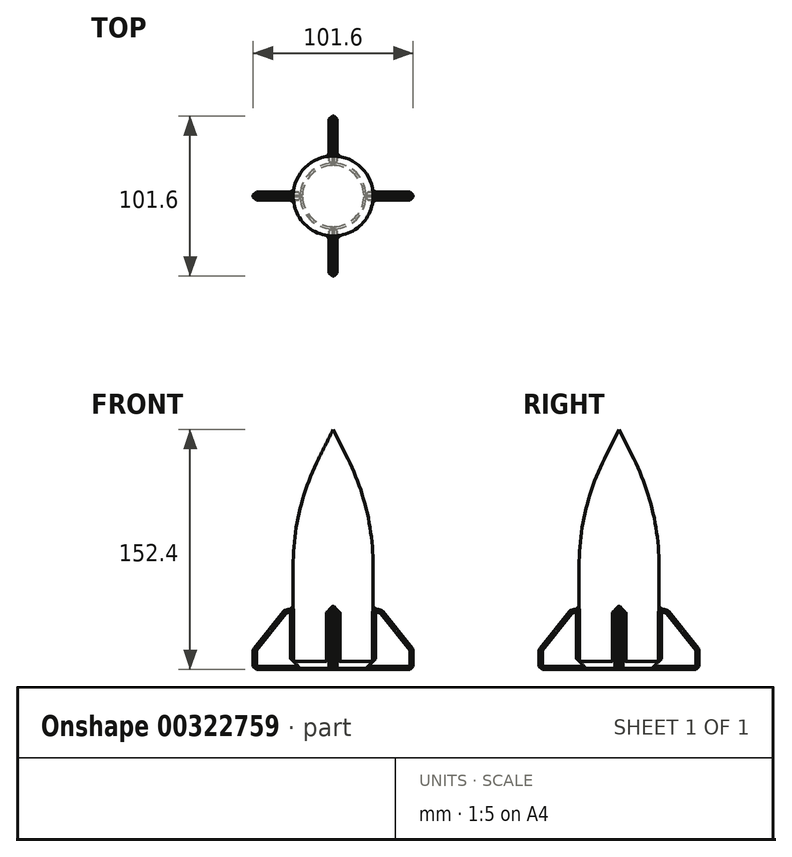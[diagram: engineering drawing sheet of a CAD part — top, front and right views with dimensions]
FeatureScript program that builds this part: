
annotation { "Feature Type Name" : "Feature", "Feature Type Description" : "" }
export const myFeature = defineFeature(function(context is Context, id is Id, definition is map)
    precondition{}
    {
        {
            var Q0;
            Q0=qCreatedBy(makeId("Top.planeOp"),FACE);
            var sketch = newSketch(context, id + "F0", { "sketchPlane" : qUnion([Q0])});
            skLineSegment(sketch, "E0.bottom", {"start": v(-25.4, 25.4) * mm, "end": v(25.4, 25.4) * mm});
            skLineSegment(sketch, "E0.top", {"start": v(-25.4, -25.4) * mm, "end": v(25.4, -25.4) * mm});
            skLineSegment(sketch, "E0.left", {"start": v(-25.4, 25.4) * mm, "end": v(-25.4, -25.4) * mm});
            skLineSegment(sketch, "E0.right", {"start": v(25.4, 25.4) * mm, "end": v(25.4, -25.4) * mm});
            skSolve(sketch);
        }
        {
            var Q0;
            Q0 = qSketchRegion(id + "F0", true);
            extrude(context, id + "F1", {"entities" : qUnion([Q0]), "depth" : 152.4 * mm});
        }
        {
            var Q0;
            Q0=makeQuery(id+"F1.opExtrude","SWEPT_FACE",FACE,{"disambiguationData":[OSD([sQuery(id+"F0.wireOp",EDGE,"E0.bottom")])]});
            var sketch = newSketch(context, id + "F2", { "sketchPlane" : qUnion([Q0])});
            skLineSegment(sketch, "E1.bottom", {"start": v(-2.54, 0) * mm, "end": v(2.54, 0) * mm});
            skLineSegment(sketch, "E1.top", {"start": v(-2.54, 38.1) * mm, "end": v(2.54, 38.1) * mm});
            skLineSegment(sketch, "E1.left", {"start": v(-2.54, 0) * mm, "end": v(-2.54, 38.1) * mm});
            skLineSegment(sketch, "E1.right", {"start": v(2.54, 0) * mm, "end": v(2.54, 38.1) * mm});
            skSolve(sketch);
        }
        {
            var Q0;
            Q0 = qSketchRegion(id + "F2", true);
            extrude(context, id + "F3", {"entities" : qUnion([Q0]), "operationType" : NewBodyOperationType.ADD, "depth" : 25.4 * mm});
        }
        {
            var Q0;
            Q0=makeQuery(id+"F3.opExtrude","CAP_EDGE",EDGE,{"disambiguationData":[OSD([sQuery(id+"F2.wireOp",EDGE,"E1.top")])],"isStart":false});
            chamfer(context, id + "F4", {"entities" : qUnion([Q0]), "chamferType" : ChamferType.TWO_OFFSETS, "width1" : 20.32 * mm, "oppositeDirection" : false, "width2" : 25.4 * mm, "tangentPropagation" : true});
        }
        {
            var Q0;
            Q0=makeQuery(id+"F1.opExtrude","SWEPT_FACE",FACE,{"disambiguationData":[OSD([sQuery(id+"F0.wireOp",EDGE,"E0.left")])]});
            var sketch = newSketch(context, id + "F5", { "sketchPlane" : qUnion([Q0])});
            skLineSegment(sketch, "E2.bottom", {"start": v(-2.54, 0) * mm, "end": v(2.54, 0) * mm});
            skLineSegment(sketch, "E2.top", {"start": v(-2.54, 38.1) * mm, "end": v(2.54, 38.1) * mm});
            skLineSegment(sketch, "E2.left", {"start": v(-2.54, 0) * mm, "end": v(-2.54, 38.1) * mm});
            skLineSegment(sketch, "E2.right", {"start": v(2.54, 0) * mm, "end": v(2.54, 38.1) * mm});
            skSolve(sketch);
        }
        {
            var Q0;
            Q0 = qSketchRegion(id + "F5", true);
            extrude(context, id + "F6", {"entities" : qUnion([Q0]), "operationType" : NewBodyOperationType.ADD, "depth" : 25.4 * mm});
        }
        {
            var Q0;
            Q0=makeQuery(id+"F6.opExtrude","CAP_EDGE",EDGE,{"disambiguationData":[OSD([sQuery(id+"F5.wireOp",EDGE,"E2.top")])],"isStart":false});
            chamfer(context, id + "F7", {"entities" : qUnion([Q0]), "chamferType" : ChamferType.TWO_OFFSETS, "width1" : 20.32 * mm, "oppositeDirection" : false, "width2" : 25.4 * mm, "tangentPropagation" : true});
        }
        {
            var Q0;
            Q0=makeQuery(id+"F1.opExtrude","SWEPT_FACE",FACE,{"disambiguationData":[OSD([sQuery(id+"F0.wireOp",EDGE,"E0.top")])]});
            var sketch = newSketch(context, id + "F8", { "sketchPlane" : qUnion([Q0])});
            skLineSegment(sketch, "E3.bottom", {"start": v(-2.54, 0) * mm, "end": v(2.54, 0) * mm});
            skLineSegment(sketch, "E3.top", {"start": v(-2.54, 38.1) * mm, "end": v(2.54, 38.1) * mm});
            skLineSegment(sketch, "E3.left", {"start": v(-2.54, 0) * mm, "end": v(-2.54, 38.1) * mm});
            skLineSegment(sketch, "E3.right", {"start": v(2.54, 0) * mm, "end": v(2.54, 38.1) * mm});
            skSolve(sketch);
        }
        {
            var Q0;
            Q0 = qSketchRegion(id + "F8", true);
            extrude(context, id + "F9", {"entities" : qUnion([Q0]), "operationType" : NewBodyOperationType.ADD, "depth" : 25.4 * mm});
        }
        {
            var Q0;
            Q0=makeQuery(id+"F9.opExtrude","CAP_EDGE",EDGE,{"disambiguationData":[OSD([sQuery(id+"F8.wireOp",EDGE,"E3.top")])],"isStart":false});
            chamfer(context, id + "F10", {"entities" : qUnion([Q0]), "chamferType" : ChamferType.TWO_OFFSETS, "width1" : 20.32 * mm, "oppositeDirection" : false, "width2" : 25.4 * mm, "tangentPropagation" : true});
        }
        {
            var Q0;
            Q0=makeQuery(id+"F1.opExtrude","SWEPT_FACE",FACE,{"disambiguationData":[OSD([sQuery(id+"F0.wireOp",EDGE,"E0.right")])]});
            var sketch = newSketch(context, id + "F11", { "sketchPlane" : qUnion([Q0])});
            skLineSegment(sketch, "E4.bottom", {"start": v(-2.54, 0) * mm, "end": v(2.54, 0) * mm});
            skLineSegment(sketch, "E4.top", {"start": v(-2.54, 38.1) * mm, "end": v(2.54, 38.1) * mm});
            skLineSegment(sketch, "E4.left", {"start": v(-2.54, 0) * mm, "end": v(-2.54, 38.1) * mm});
            skLineSegment(sketch, "E4.right", {"start": v(2.54, 0) * mm, "end": v(2.54, 38.1) * mm});
            skSolve(sketch);
        }
        {
            var Q0;
            Q0 = qSketchRegion(id + "F11", true);
            extrude(context, id + "F12", {"entities" : qUnion([Q0]), "operationType" : NewBodyOperationType.ADD, "depth" : 25.4 * mm});
        }
        {
            var Q0;
            Q0=makeQuery(id+"F12.opExtrude","CAP_EDGE",EDGE,{"disambiguationData":[OSD([sQuery(id+"F11.wireOp",EDGE,"E4.top")])],"isStart":false});
            chamfer(context, id + "F13", {"entities" : qUnion([Q0]), "chamferType" : ChamferType.TWO_OFFSETS, "width1" : 20.32 * mm, "oppositeDirection" : false, "width2" : 25.4 * mm, "tangentPropagation" : true});
        }
        {
            var Q0;
            Q0=makeQuery(id+"F1.opExtrude","SWEPT_EDGE",EDGE,{"disambiguationData":[OSD([sQuery(id+"F0.wireOp",EDGE,"E0.top"),sQuery(id+"F0.wireOp",EDGE,"E0.right")])]});
            var Q1;
            Q1=makeQuery(id+"F1.opExtrude","SWEPT_EDGE",EDGE,{"disambiguationData":[OSD([sQuery(id+"F0.wireOp",EDGE,"E0.top"),sQuery(id+"F0.wireOp",EDGE,"E0.left")])]});
            var Q2;
            Q2=makeQuery(id+"F1.opExtrude","SWEPT_EDGE",EDGE,{"disambiguationData":[OSD([sQuery(id+"F0.wireOp",EDGE,"E0.bottom"),sQuery(id+"F0.wireOp",EDGE,"E0.left")])]});
            var Q3;
            Q3=makeQuery(id+"F1.opExtrude","SWEPT_EDGE",EDGE,{"disambiguationData":[OSD([sQuery(id+"F0.wireOp",EDGE,"E0.bottom"),sQuery(id+"F0.wireOp",EDGE,"E0.right")])]});
            fillet(context, id + "F14", {"entities" : qUnion([Q0, Q1, Q2, Q3]), "radius" : 25.4 * mm, "tangentPropagation" : true, "allowEdgeOverflow" : false});
        }
        {
            var Q0;
            {var subQ0=sQuery(id+"F0.wireOp",EDGE,"E0.left");var subQ1=sQuery(id+"F0.wireOp",EDGE,"E0.bottom");Q0=makeQuery(id+"F14.opFillet","BLEND_EDGE",EDGE,{"blendedFrom":[makeQuery(id+"F1.opExtrude","SWEPT_EDGE",EDGE,{"disambiguationData":[OSD([subQ1,subQ0])]}),makeQuery(id+"F1.opExtrude","CAP_FACE",FACE,{"disambiguationData":[OSD([subQ1,sQuery(id+"F0.wireOp",EDGE,"E0.top"),subQ0,sQuery(id+"F0.wireOp",EDGE,"E0.right")])],"isStart":false})],"blendedInto":[makeQuery(id+"F1.opExtrude","CAP_FACE",FACE,{"disambiguationData":[OSD([subQ1,sQuery(id+"F0.wireOp",EDGE,"E0.top"),subQ0,sQuery(id+"F0.wireOp",EDGE,"E0.right")])],"isStart":false})]});}
            chamfer(context, id + "F15", {"entities" : qUnion([Q0]), "chamferType" : ChamferType.TWO_OFFSETS, "width1" : 25.4 * mm, "oppositeDirection" : false, "width2" : 50.8 * mm, "tangentPropagation" : true});
        }
        {
            var Q0;
            {var subQ0=sQuery(id+"F0.wireOp",EDGE,"E0.right");var subQ1=sQuery(id+"F0.wireOp",EDGE,"E0.bottom");var subQ2=sQuery(id+"F0.wireOp",EDGE,"E0.left");Q0=makeQuery(id+"F15.opChamfer","BLEND_EDGE",EDGE,{"blendedFrom":[makeQuery(id+"F14.opFillet","BLEND_EDGE",EDGE,{"blendedFrom":[makeQuery(id+"F1.opExtrude","SWEPT_EDGE",EDGE,{"disambiguationData":[OSD([subQ1,subQ2])]}),makeQuery(id+"F1.opExtrude","CAP_FACE",FACE,{"disambiguationData":[OSD([subQ1,sQuery(id+"F0.wireOp",EDGE,"E0.top"),subQ2,subQ0])],"isStart":false})],"blendedInto":[makeQuery(id+"F1.opExtrude","CAP_FACE",FACE,{"disambiguationData":[OSD([subQ1,sQuery(id+"F0.wireOp",EDGE,"E0.top"),subQ2,subQ0])],"isStart":false})]}),makeQuery(id+"F14.opFillet","BLEND_FACE",FACE,{"disambiguationData":[OSD([subQ1,subQ0])]})],"blendedInto":[makeQuery(id+"F14.opFillet","BLEND_FACE",FACE,{"disambiguationData":[OSD([subQ1,subQ0])]})]});}
            fillet(context, id + "F16", {"entities" : qUnion([Q0]), "radius" : 152.4 * mm, "tangentPropagation" : true, "allowEdgeOverflow" : false});
        }
        {
            var Q0;
            {var subQ0=sQuery(id+"F8.wireOp",EDGE,"E3.top");Q0=makeQuery(id+"F10.opChamfer","BLEND_EDGE",EDGE,{"blendedFrom":[makeQuery(id+"F9.opExtrude","CAP_EDGE",EDGE,{"disambiguationData":[OSD([subQ0])],"isStart":false}),makeQuery(id+"F9.opExtrude","SWEPT_FACE",FACE,{"disambiguationData":[OSD([subQ0])]})],"blendedInto":[makeQuery(id+"F9.opExtrude","SWEPT_FACE",FACE,{"disambiguationData":[OSD([subQ0])]})]});}
            chamfer(context, id + "F17", {"entities" : qUnion([Q0]), "width" : 2.54 * mm, "tangentPropagation" : true});
        }
        {
            var Q0;
            {var subQ0=sQuery(id+"F11.wireOp",EDGE,"E4.top");Q0=makeQuery(id+"F13.opChamfer","BLEND_EDGE",EDGE,{"blendedFrom":[makeQuery(id+"F12.opExtrude","CAP_EDGE",EDGE,{"disambiguationData":[OSD([subQ0])],"isStart":false}),makeQuery(id+"F12.opExtrude","SWEPT_FACE",FACE,{"disambiguationData":[OSD([subQ0])]})],"blendedInto":[makeQuery(id+"F12.opExtrude","SWEPT_FACE",FACE,{"disambiguationData":[OSD([subQ0])]})]});}
            chamfer(context, id + "F18", {"entities" : qUnion([Q0]), "width" : 2.54 * mm, "tangentPropagation" : true});
        }
        {
            var Q0;
            {var subQ0=sQuery(id+"F2.wireOp",EDGE,"E1.top");Q0=makeQuery(id+"F4.opChamfer","BLEND_EDGE",EDGE,{"blendedFrom":[makeQuery(id+"F3.opExtrude","CAP_EDGE",EDGE,{"disambiguationData":[OSD([subQ0])],"isStart":false}),makeQuery(id+"F3.opExtrude","SWEPT_FACE",FACE,{"disambiguationData":[OSD([subQ0])]})],"blendedInto":[makeQuery(id+"F3.opExtrude","SWEPT_FACE",FACE,{"disambiguationData":[OSD([subQ0])]})]});}
            var Q1;
            {var subQ0=sQuery(id+"F5.wireOp",EDGE,"E2.top");Q1=makeQuery(id+"F7.opChamfer","BLEND_EDGE",EDGE,{"blendedFrom":[makeQuery(id+"F6.opExtrude","CAP_EDGE",EDGE,{"disambiguationData":[OSD([subQ0])],"isStart":false}),makeQuery(id+"F6.opExtrude","SWEPT_FACE",FACE,{"disambiguationData":[OSD([subQ0])]})],"blendedInto":[makeQuery(id+"F6.opExtrude","SWEPT_FACE",FACE,{"disambiguationData":[OSD([subQ0])]})]});}
            chamfer(context, id + "F19", {"entities" : qUnion([Q0, Q1]), "width" : 2.54 * mm, "tangentPropagation" : true});
        }
        {
            var Q0;
            {var subQ0=sQuery(id+"F0.wireOp",EDGE,"E0.left");var subQ1=sQuery(id+"F0.wireOp",EDGE,"E0.bottom");Q0=makeQuery(id+"F14.opFillet","BLEND_EDGE",EDGE,{"blendedFrom":[makeQuery(id+"F1.opExtrude","SWEPT_EDGE",EDGE,{"disambiguationData":[OSD([subQ1,subQ0])]}),makeQuery(id+"F12.boolean.opBoolean","MERGE",FACE,{"derivedFrom":[makeQuery(id+"F9.boolean.opBoolean","MERGE",FACE,{"derivedFrom":[makeQuery(id+"F6.boolean.opBoolean","MERGE",FACE,{"derivedFrom":[makeQuery(id+"F3.boolean.opBoolean","MERGE",FACE,{"derivedFrom":[makeQuery(id+"F1.opExtrude","CAP_FACE",FACE,{"disambiguationData":[OSD([subQ1,sQuery(id+"F0.wireOp",EDGE,"E0.top"),subQ0,sQuery(id+"F0.wireOp",EDGE,"E0.right")])],"isStart":true}),makeQuery(id+"F3.opExtrude","SWEPT_FACE",FACE,{"disambiguationData":[OSD([sQuery(id+"F2.wireOp",EDGE,"E1.bottom")])]})]}),makeQuery(id+"F6.opExtrude","SWEPT_FACE",FACE,{"disambiguationData":[OSD([sQuery(id+"F5.wireOp",EDGE,"E2.bottom")])]})]}),makeQuery(id+"F9.opExtrude","SWEPT_FACE",FACE,{"disambiguationData":[OSD([sQuery(id+"F8.wireOp",EDGE,"E3.bottom")])]})]}),makeQuery(id+"F12.opExtrude","SWEPT_FACE",FACE,{"disambiguationData":[OSD([sQuery(id+"F11.wireOp",EDGE,"E4.bottom")])]})]})],"blendedInto":[makeQuery(id+"F12.boolean.opBoolean","MERGE",FACE,{"derivedFrom":[makeQuery(id+"F9.boolean.opBoolean","MERGE",FACE,{"derivedFrom":[makeQuery(id+"F6.boolean.opBoolean","MERGE",FACE,{"derivedFrom":[makeQuery(id+"F3.boolean.opBoolean","MERGE",FACE,{"derivedFrom":[makeQuery(id+"F1.opExtrude","CAP_FACE",FACE,{"disambiguationData":[OSD([subQ1,sQuery(id+"F0.wireOp",EDGE,"E0.top"),subQ0,sQuery(id+"F0.wireOp",EDGE,"E0.right")])],"isStart":true}),makeQuery(id+"F3.opExtrude","SWEPT_FACE",FACE,{"disambiguationData":[OSD([sQuery(id+"F2.wireOp",EDGE,"E1.bottom")])]})]}),makeQuery(id+"F6.opExtrude","SWEPT_FACE",FACE,{"disambiguationData":[OSD([sQuery(id+"F5.wireOp",EDGE,"E2.bottom")])]})]}),makeQuery(id+"F9.opExtrude","SWEPT_FACE",FACE,{"disambiguationData":[OSD([sQuery(id+"F8.wireOp",EDGE,"E3.bottom")])]})]}),makeQuery(id+"F12.opExtrude","SWEPT_FACE",FACE,{"disambiguationData":[OSD([sQuery(id+"F11.wireOp",EDGE,"E4.bottom")])]})]})]});}
            var Q1;
            {var subQ0=sQuery(id+"F0.wireOp",EDGE,"E0.left");var subQ1=sQuery(id+"F0.wireOp",EDGE,"E0.top");Q1=makeQuery(id+"F14.opFillet","BLEND_EDGE",EDGE,{"blendedFrom":[makeQuery(id+"F1.opExtrude","SWEPT_EDGE",EDGE,{"disambiguationData":[OSD([subQ1,subQ0])]}),makeQuery(id+"F12.boolean.opBoolean","MERGE",FACE,{"derivedFrom":[makeQuery(id+"F9.boolean.opBoolean","MERGE",FACE,{"derivedFrom":[makeQuery(id+"F6.boolean.opBoolean","MERGE",FACE,{"derivedFrom":[makeQuery(id+"F3.boolean.opBoolean","MERGE",FACE,{"derivedFrom":[makeQuery(id+"F1.opExtrude","CAP_FACE",FACE,{"disambiguationData":[OSD([sQuery(id+"F0.wireOp",EDGE,"E0.bottom"),subQ1,subQ0,sQuery(id+"F0.wireOp",EDGE,"E0.right")])],"isStart":true}),makeQuery(id+"F3.opExtrude","SWEPT_FACE",FACE,{"disambiguationData":[OSD([sQuery(id+"F2.wireOp",EDGE,"E1.bottom")])]})]}),makeQuery(id+"F6.opExtrude","SWEPT_FACE",FACE,{"disambiguationData":[OSD([sQuery(id+"F5.wireOp",EDGE,"E2.bottom")])]})]}),makeQuery(id+"F9.opExtrude","SWEPT_FACE",FACE,{"disambiguationData":[OSD([sQuery(id+"F8.wireOp",EDGE,"E3.bottom")])]})]}),makeQuery(id+"F12.opExtrude","SWEPT_FACE",FACE,{"disambiguationData":[OSD([sQuery(id+"F11.wireOp",EDGE,"E4.bottom")])]})]})],"blendedInto":[makeQuery(id+"F12.boolean.opBoolean","MERGE",FACE,{"derivedFrom":[makeQuery(id+"F9.boolean.opBoolean","MERGE",FACE,{"derivedFrom":[makeQuery(id+"F6.boolean.opBoolean","MERGE",FACE,{"derivedFrom":[makeQuery(id+"F3.boolean.opBoolean","MERGE",FACE,{"derivedFrom":[makeQuery(id+"F1.opExtrude","CAP_FACE",FACE,{"disambiguationData":[OSD([sQuery(id+"F0.wireOp",EDGE,"E0.bottom"),subQ1,subQ0,sQuery(id+"F0.wireOp",EDGE,"E0.right")])],"isStart":true}),makeQuery(id+"F3.opExtrude","SWEPT_FACE",FACE,{"disambiguationData":[OSD([sQuery(id+"F2.wireOp",EDGE,"E1.bottom")])]})]}),makeQuery(id+"F6.opExtrude","SWEPT_FACE",FACE,{"disambiguationData":[OSD([sQuery(id+"F5.wireOp",EDGE,"E2.bottom")])]})]}),makeQuery(id+"F9.opExtrude","SWEPT_FACE",FACE,{"disambiguationData":[OSD([sQuery(id+"F8.wireOp",EDGE,"E3.bottom")])]})]}),makeQuery(id+"F12.opExtrude","SWEPT_FACE",FACE,{"disambiguationData":[OSD([sQuery(id+"F11.wireOp",EDGE,"E4.bottom")])]})]})]});}
            var Q2;
            {var subQ0=sQuery(id+"F0.wireOp",EDGE,"E0.right");var subQ1=sQuery(id+"F0.wireOp",EDGE,"E0.top");Q2=makeQuery(id+"F14.opFillet","BLEND_EDGE",EDGE,{"blendedFrom":[makeQuery(id+"F1.opExtrude","SWEPT_EDGE",EDGE,{"disambiguationData":[OSD([subQ1,subQ0])]}),makeQuery(id+"F12.boolean.opBoolean","MERGE",FACE,{"derivedFrom":[makeQuery(id+"F9.boolean.opBoolean","MERGE",FACE,{"derivedFrom":[makeQuery(id+"F6.boolean.opBoolean","MERGE",FACE,{"derivedFrom":[makeQuery(id+"F3.boolean.opBoolean","MERGE",FACE,{"derivedFrom":[makeQuery(id+"F1.opExtrude","CAP_FACE",FACE,{"disambiguationData":[OSD([sQuery(id+"F0.wireOp",EDGE,"E0.bottom"),subQ1,sQuery(id+"F0.wireOp",EDGE,"E0.left"),subQ0])],"isStart":true}),makeQuery(id+"F3.opExtrude","SWEPT_FACE",FACE,{"disambiguationData":[OSD([sQuery(id+"F2.wireOp",EDGE,"E1.bottom")])]})]}),makeQuery(id+"F6.opExtrude","SWEPT_FACE",FACE,{"disambiguationData":[OSD([sQuery(id+"F5.wireOp",EDGE,"E2.bottom")])]})]}),makeQuery(id+"F9.opExtrude","SWEPT_FACE",FACE,{"disambiguationData":[OSD([sQuery(id+"F8.wireOp",EDGE,"E3.bottom")])]})]}),makeQuery(id+"F12.opExtrude","SWEPT_FACE",FACE,{"disambiguationData":[OSD([sQuery(id+"F11.wireOp",EDGE,"E4.bottom")])]})]})],"blendedInto":[makeQuery(id+"F12.boolean.opBoolean","MERGE",FACE,{"derivedFrom":[makeQuery(id+"F9.boolean.opBoolean","MERGE",FACE,{"derivedFrom":[makeQuery(id+"F6.boolean.opBoolean","MERGE",FACE,{"derivedFrom":[makeQuery(id+"F3.boolean.opBoolean","MERGE",FACE,{"derivedFrom":[makeQuery(id+"F1.opExtrude","CAP_FACE",FACE,{"disambiguationData":[OSD([sQuery(id+"F0.wireOp",EDGE,"E0.bottom"),subQ1,sQuery(id+"F0.wireOp",EDGE,"E0.left"),subQ0])],"isStart":true}),makeQuery(id+"F3.opExtrude","SWEPT_FACE",FACE,{"disambiguationData":[OSD([sQuery(id+"F2.wireOp",EDGE,"E1.bottom")])]})]}),makeQuery(id+"F6.opExtrude","SWEPT_FACE",FACE,{"disambiguationData":[OSD([sQuery(id+"F5.wireOp",EDGE,"E2.bottom")])]})]}),makeQuery(id+"F9.opExtrude","SWEPT_FACE",FACE,{"disambiguationData":[OSD([sQuery(id+"F8.wireOp",EDGE,"E3.bottom")])]})]}),makeQuery(id+"F12.opExtrude","SWEPT_FACE",FACE,{"disambiguationData":[OSD([sQuery(id+"F11.wireOp",EDGE,"E4.bottom")])]})]})]});}
            var Q3;
            {var subQ0=sQuery(id+"F0.wireOp",EDGE,"E0.right");var subQ1=sQuery(id+"F0.wireOp",EDGE,"E0.bottom");Q3=makeQuery(id+"F14.opFillet","BLEND_EDGE",EDGE,{"blendedFrom":[makeQuery(id+"F1.opExtrude","SWEPT_EDGE",EDGE,{"disambiguationData":[OSD([subQ1,subQ0])]}),makeQuery(id+"F12.boolean.opBoolean","MERGE",FACE,{"derivedFrom":[makeQuery(id+"F9.boolean.opBoolean","MERGE",FACE,{"derivedFrom":[makeQuery(id+"F6.boolean.opBoolean","MERGE",FACE,{"derivedFrom":[makeQuery(id+"F3.boolean.opBoolean","MERGE",FACE,{"derivedFrom":[makeQuery(id+"F1.opExtrude","CAP_FACE",FACE,{"disambiguationData":[OSD([subQ1,sQuery(id+"F0.wireOp",EDGE,"E0.top"),sQuery(id+"F0.wireOp",EDGE,"E0.left"),subQ0])],"isStart":true}),makeQuery(id+"F3.opExtrude","SWEPT_FACE",FACE,{"disambiguationData":[OSD([sQuery(id+"F2.wireOp",EDGE,"E1.bottom")])]})]}),makeQuery(id+"F6.opExtrude","SWEPT_FACE",FACE,{"disambiguationData":[OSD([sQuery(id+"F5.wireOp",EDGE,"E2.bottom")])]})]}),makeQuery(id+"F9.opExtrude","SWEPT_FACE",FACE,{"disambiguationData":[OSD([sQuery(id+"F8.wireOp",EDGE,"E3.bottom")])]})]}),makeQuery(id+"F12.opExtrude","SWEPT_FACE",FACE,{"disambiguationData":[OSD([sQuery(id+"F11.wireOp",EDGE,"E4.bottom")])]})]})],"blendedInto":[makeQuery(id+"F12.boolean.opBoolean","MERGE",FACE,{"derivedFrom":[makeQuery(id+"F9.boolean.opBoolean","MERGE",FACE,{"derivedFrom":[makeQuery(id+"F6.boolean.opBoolean","MERGE",FACE,{"derivedFrom":[makeQuery(id+"F3.boolean.opBoolean","MERGE",FACE,{"derivedFrom":[makeQuery(id+"F1.opExtrude","CAP_FACE",FACE,{"disambiguationData":[OSD([subQ1,sQuery(id+"F0.wireOp",EDGE,"E0.top"),sQuery(id+"F0.wireOp",EDGE,"E0.left"),subQ0])],"isStart":true}),makeQuery(id+"F3.opExtrude","SWEPT_FACE",FACE,{"disambiguationData":[OSD([sQuery(id+"F2.wireOp",EDGE,"E1.bottom")])]})]}),makeQuery(id+"F6.opExtrude","SWEPT_FACE",FACE,{"disambiguationData":[OSD([sQuery(id+"F5.wireOp",EDGE,"E2.bottom")])]})]}),makeQuery(id+"F9.opExtrude","SWEPT_FACE",FACE,{"disambiguationData":[OSD([sQuery(id+"F8.wireOp",EDGE,"E3.bottom")])]})]}),makeQuery(id+"F12.opExtrude","SWEPT_FACE",FACE,{"disambiguationData":[OSD([sQuery(id+"F11.wireOp",EDGE,"E4.bottom")])]})]})]});}
            chamfer(context, id + "F20", {"entities" : qUnion([Q0, Q1, Q2, Q3]), "width" : 5.08 * mm, "tangentPropagation" : true});
        }
        {
            var Q0;
            Q0=makeQuery(id+"F9.opExtrude","SWEPT_FACE",FACE,{"disambiguationData":[OSD([sQuery(id+"F8.wireOp",EDGE,"E3.top")])]});
            var Q1;
            Q1=makeQuery(id+"F17.opChamfer","BLEND_FACE",FACE,{"disambiguationData":[OSD([sQuery(id+"F8.wireOp",EDGE,"E3.top")])]});
            var Q2;
            Q2=makeQuery(id+"F10.opChamfer","BLEND_FACE",FACE,{"disambiguationData":[OSD([sQuery(id+"F8.wireOp",EDGE,"E3.top")])]});
            var Q3;
            Q3=makeQuery(id+"F9.opExtrude","CAP_FACE",FACE,{"disambiguationData":[OSD([sQuery(id+"F8.wireOp",EDGE,"E3.bottom"),sQuery(id+"F8.wireOp",EDGE,"E3.top"),sQuery(id+"F8.wireOp",EDGE,"E3.left"),sQuery(id+"F8.wireOp",EDGE,"E3.right")])],"isStart":false});
            var Q4;
            Q4=makeQuery(id+"F12.boolean.opBoolean","MERGE",FACE,{"derivedFrom":[makeQuery(id+"F9.boolean.opBoolean","MERGE",FACE,{"derivedFrom":[makeQuery(id+"F6.boolean.opBoolean","MERGE",FACE,{"derivedFrom":[makeQuery(id+"F3.boolean.opBoolean","MERGE",FACE,{"derivedFrom":[makeQuery(id+"F1.opExtrude","CAP_FACE",FACE,{"disambiguationData":[OSD([sQuery(id+"F0.wireOp",EDGE,"E0.bottom"),sQuery(id+"F0.wireOp",EDGE,"E0.top"),sQuery(id+"F0.wireOp",EDGE,"E0.left"),sQuery(id+"F0.wireOp",EDGE,"E0.right")])],"isStart":true}),makeQuery(id+"F3.opExtrude","SWEPT_FACE",FACE,{"disambiguationData":[OSD([sQuery(id+"F2.wireOp",EDGE,"E1.bottom")])]})]}),makeQuery(id+"F6.opExtrude","SWEPT_FACE",FACE,{"disambiguationData":[OSD([sQuery(id+"F5.wireOp",EDGE,"E2.bottom")])]})]}),makeQuery(id+"F9.opExtrude","SWEPT_FACE",FACE,{"disambiguationData":[OSD([sQuery(id+"F8.wireOp",EDGE,"E3.bottom")])]})]}),makeQuery(id+"F12.opExtrude","SWEPT_FACE",FACE,{"disambiguationData":[OSD([sQuery(id+"F11.wireOp",EDGE,"E4.bottom")])]})]});
            var Q5;
            Q5=makeQuery(id+"F6.opExtrude","CAP_FACE",FACE,{"disambiguationData":[OSD([sQuery(id+"F5.wireOp",EDGE,"E2.bottom"),sQuery(id+"F5.wireOp",EDGE,"E2.top"),sQuery(id+"F5.wireOp",EDGE,"E2.left"),sQuery(id+"F5.wireOp",EDGE,"E2.right")])],"isStart":false});
            var Q6;
            Q6=makeQuery(id+"F7.opChamfer","BLEND_FACE",FACE,{"disambiguationData":[OSD([sQuery(id+"F5.wireOp",EDGE,"E2.top")])]});
            var Q7;
            Q7=makeQuery(id+"F19.opChamfer","BLEND_FACE",FACE,{"disambiguationData":[OSD([sQuery(id+"F5.wireOp",EDGE,"E2.top")])]});
            var Q8;
            Q8=makeQuery(id+"F6.opExtrude","SWEPT_FACE",FACE,{"disambiguationData":[OSD([sQuery(id+"F5.wireOp",EDGE,"E2.top")])]});
            var Q9;
            Q9=makeQuery(id+"F3.opExtrude","CAP_FACE",FACE,{"disambiguationData":[OSD([sQuery(id+"F2.wireOp",EDGE,"E1.bottom"),sQuery(id+"F2.wireOp",EDGE,"E1.top"),sQuery(id+"F2.wireOp",EDGE,"E1.left"),sQuery(id+"F2.wireOp",EDGE,"E1.right")])],"isStart":false});
            var Q10;
            Q10=makeQuery(id+"F4.opChamfer","BLEND_FACE",FACE,{"disambiguationData":[OSD([sQuery(id+"F2.wireOp",EDGE,"E1.top")])]});
            var Q11;
            Q11=makeQuery(id+"F19.opChamfer","BLEND_FACE",FACE,{"disambiguationData":[OSD([sQuery(id+"F2.wireOp",EDGE,"E1.top")])]});
            var Q12;
            Q12=makeQuery(id+"F3.opExtrude","SWEPT_FACE",FACE,{"disambiguationData":[OSD([sQuery(id+"F2.wireOp",EDGE,"E1.top")])]});
            var Q13;
            Q13=makeQuery(id+"F12.opExtrude","SWEPT_FACE",FACE,{"disambiguationData":[OSD([sQuery(id+"F11.wireOp",EDGE,"E4.top")])]});
            var Q14;
            Q14=makeQuery(id+"F18.opChamfer","BLEND_FACE",FACE,{"disambiguationData":[OSD([sQuery(id+"F11.wireOp",EDGE,"E4.top")])]});
            var Q15;
            Q15=makeQuery(id+"F13.opChamfer","BLEND_FACE",FACE,{"disambiguationData":[OSD([sQuery(id+"F11.wireOp",EDGE,"E4.top")])]});
            var Q16;
            Q16=makeQuery(id+"F12.opExtrude","CAP_FACE",FACE,{"disambiguationData":[OSD([sQuery(id+"F11.wireOp",EDGE,"E4.bottom"),sQuery(id+"F11.wireOp",EDGE,"E4.top"),sQuery(id+"F11.wireOp",EDGE,"E4.left"),sQuery(id+"F11.wireOp",EDGE,"E4.right")])],"isStart":false});
            chamfer(context, id + "F21", {"entities" : qUnion([Q0, Q1, Q2, Q3, Q4, Q5, Q6, Q7, Q8, Q9, Q10, Q11, Q12, Q13, Q14, Q15, Q16]), "width" : 2.03 * mm, "tangentPropagation" : true});
        }
    });
